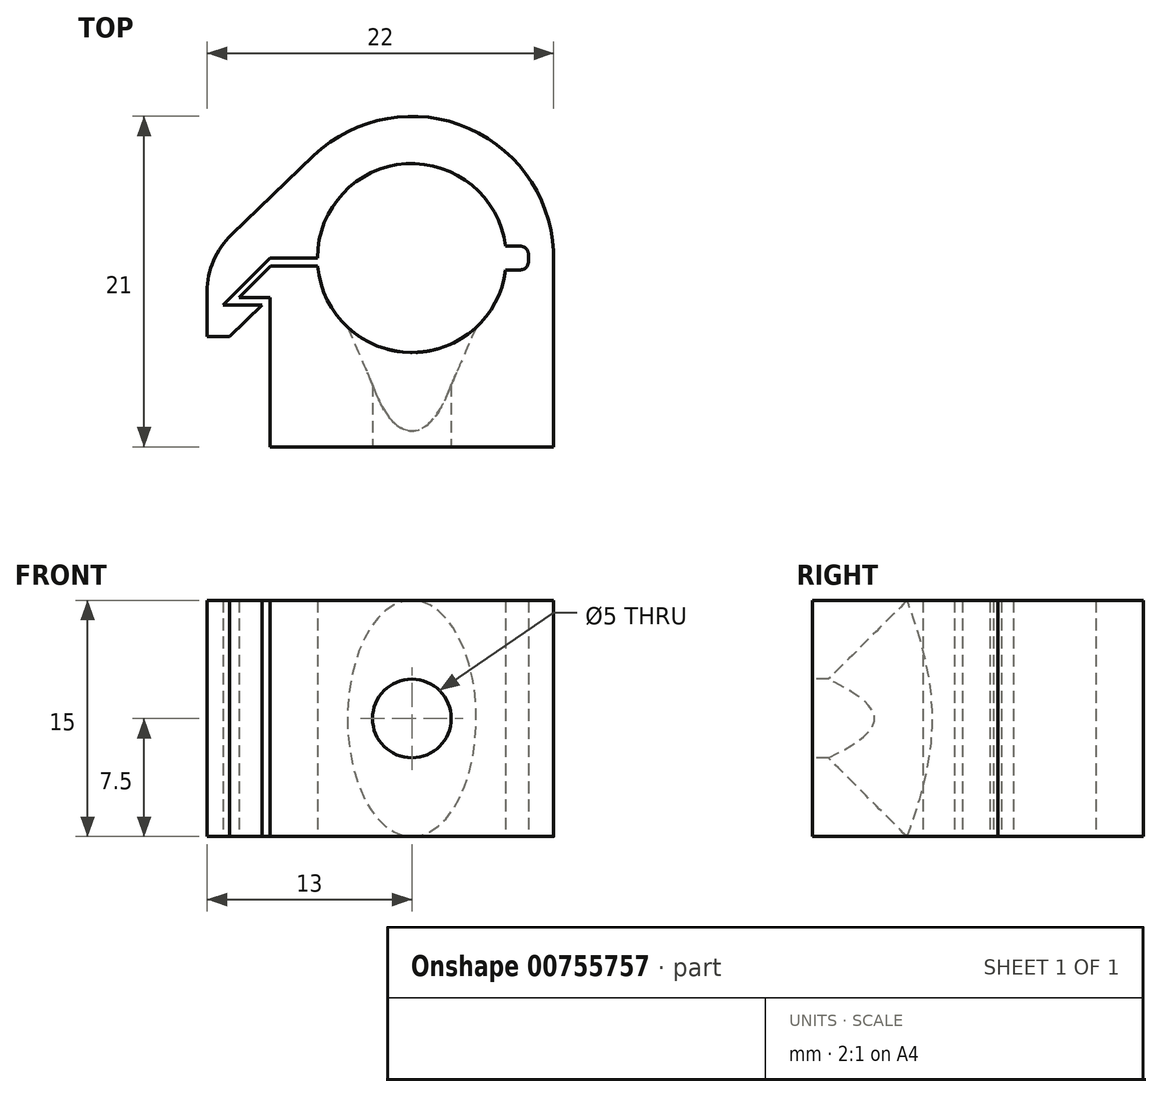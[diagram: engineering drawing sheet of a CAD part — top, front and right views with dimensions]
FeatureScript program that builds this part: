
annotation { "Feature Type Name" : "Feature", "Feature Type Description" : "" }
export const myFeature = defineFeature(function(context is Context, id is Id, definition is map)
    precondition{}
    {
        {
            var Q0;
            Q0=qCreatedBy(makeId("Top.planeOp"),FACE);
            var sketch = newSketch(context, id + "F0", { "sketchPlane" : qUnion([Q0])});
            skArc(sketch, "E0", {"start": v(-5.98, -0.5) * mm, "mid": v(-0.13, -6) * mm, "end": v(5.95, -0.75) * mm});
            skArc(sketch, "E1.0", {"start": v(9, -0.23) * mm, "mid": v(3.64, 8.23) * mm, "end": v(-6.23, 6.5) * mm});
            skLineSegment(sketch, "E2", {"start": v(-9, 0) * mm, "end": v(-6, 0) * mm});
            skLineSegment(sketch, "E3.0", {"start": v(-8.99, -0.5) * mm, "end": v(-5.98, -0.5) * mm});
            skLineSegment(sketch, "E4.top", {"start": v(-9, -12) * mm, "end": v(9, -12) * mm});
            skLineSegment(sketch, "E5.top", {"start": v(-8.99, -2.5) * mm, "end": v(-10.99, -2.5) * mm});
            skLineSegment(sketch, "E5.left", {"start": v(-8.99, -0.5) * mm, "end": v(-8.99, -2.5) * mm});
            skLineSegment(sketch, "E6", {"start": v(-8.99, -0.5) * mm, "end": v(-10.99, -2.5) * mm});
            skLineSegment(sketch, "E7.bottom", {"start": v(-9, 0) * mm, "end": v(-12.52, 0) * mm});
            skLineSegment(sketch, "E7.top", {"start": v(-11.57, -5) * mm, "end": v(-13, -5) * mm});
            skLineSegment(sketch, "E7.left", {"start": v(-9, -2.5) * mm, "end": v(-9, -12) * mm});
            skLineSegment(sketch, "E7.right", {"start": v(-13, -2.13) * mm, "end": v(-13, -5) * mm});
            skLineSegment(sketch, "E8", {"start": v(-9, 0) * mm, "end": v(-12, -3) * mm});
            skLineSegment(sketch, "E9", {"start": v(-11.46, 1.48) * mm, "end": v(-6.23, 6.5) * mm});
            skPoint(sketch, "E10.visualSharp", {"position": v(-13, 0) * mm});
            skArc(sketch, "E10.filletArc", {"start": v(-11.46, 1.48) * mm, "mid": v(-12.6, -0.17) * mm, "end": v(-13, -2.13) * mm});
            skLineSegment(sketch, "E11.bottom", {"start": v(6.9, -0.75) * mm, "end": v(5.95, -0.75) * mm});
            skLineSegment(sketch, "E11.top", {"start": v(6.9, 0.75) * mm, "end": v(5.95, 0.75) * mm});
            skLineSegment(sketch, "E11.left", {"start": v(7.4, -0.25) * mm, "end": v(7.4, 0.25) * mm});
            skPoint(sketch, "E12.visualSharp", {"position": v(7.4, 0.75) * mm});
            skArc(sketch, "E12.filletArc", {"start": v(7.4, 0.25) * mm, "mid": v(7.25, 0.6) * mm, "end": v(6.9, 0.75) * mm});
            skPoint(sketch, "E13.visualSharp", {"position": v(7.4, -0.75) * mm});
            skArc(sketch, "E13.filletArc", {"start": v(6.9, -0.75) * mm, "mid": v(7.25, -0.6) * mm, "end": v(7.4, -0.25) * mm});
            skArc(sketch, "E14.trimOffspring", {"start": v(5.95, 0.75) * mm, "mid": v(-0.38, 5.99) * mm, "end": v(-6, 0) * mm});
            skLineSegment(sketch, "E15", {"start": v(-9.5, -3) * mm, "end": v(-12, -3) * mm});
            skLineSegment(sketch, "E16", {"start": v(-9.5, -3) * mm, "end": v(-11.57, -5) * mm});
            skLineSegment(sketch, "E17", {"start": v(9, -0.23) * mm, "end": v(9, -12) * mm});
            skSolve(sketch);
        }
        {
            var Q0;
            Q0=makeQuery(id+"F0.imprint","IMPRINT",FACE,{"disambiguationData":[TD([[makeQuery(id+"F0.imprint","IMPRINT",EDGE,{"derivedFrom":sQuery(id+"F0.wireOp",EDGE,"E7.top")}),-1.0]])]});
            var Q1;
            {var subQ4=sQuery(id+"F0.wireOp",EDGE,"E4.top");Q1=makeQuery(id+"F0.imprint","IMPRINT",FACE,{"disambiguationData":[TD([[makeQuery(id+"F0.imprint","IMPRINT",EDGE,{"derivedFrom":subQ4}),1.0]])]});}
            var Q2;
            Q2=makeQuery(id+"F0.imprint","IMPRINT",FACE,{"disambiguationData":[TD([[makeQuery(id+"F0.imprint","IMPRINT",EDGE,{"derivedFrom":sQuery(id+"F0.wireOp",EDGE,"E0")}),-1.0]])]});
            var Q3;
            {var subQ0=sQuery(id+"F0.wireOp",EDGE,"LmTLJ9r3-tRaW-AbCN-yqt8-uPBCqrNAEFa4");var subQ1=sQuery(id+"F0.wireOp",EDGE,"E1.0");var subQ2=makeQuery(id+"F0.imprint","INTERSECT",VERTEX,{"disambiguationData":[OD(0.0)],"derivedFrom":[subQ1,subQ0]});Q3=makeQuery(id+"F0.imprint","IMPRINT",FACE,{"disambiguationData":[TD([[makeQuery(id+"F0.imprint","IMPRINT",EDGE,{"disambiguationData":[TD([[subQ2,1.0]])],"derivedFrom":subQ1}),1.0]])]});}
            var Q4;
            {var subQ0=sQuery(id+"F0.wireOp",EDGE,"E6");var subQ1=sQuery(id+"F0.wireOp",EDGE,"E5.top");var subQ2=makeQuery(id+"F0.imprint","INTERSECT",VERTEX,{"derivedFrom":[subQ1,subQ0]});Q4=makeQuery(id+"F0.imprint","IMPRINT",FACE,{"disambiguationData":[TD([[makeQuery(id+"F0.imprint","IMPRINT",EDGE,{"disambiguationData":[TD([[subQ2,1.0]])],"derivedFrom":subQ1}),-1.0]])]});}
            var Q5;
            {var subQ0=sQuery(id+"F0.wireOp",EDGE,"E5.left");Q5=makeQuery(id+"F0.imprint","IMPRINT",FACE,{"disambiguationData":[TD([[makeQuery(id+"F0.imprint","IMPRINT",EDGE,{"derivedFrom":subQ0}),-1.0]])]});}
            extrude(context, id + "F1", {"entities" : qUnion([Q0, Q1, Q2, Q3, Q4, Q5]), "depth" : 15 * mm, "offsetDistance" : 25 * mm, "symmetric" : true});
        }
        {
            var Q0;
            Q0=makeQuery(id+"F1.opExtrude","SWEPT_FACE",FACE,{"disambiguationData":[OSD([sQuery(id+"F0.wireOp",EDGE,"E4.top")])]});
            var sketch = newSketch(context, id + "F2", { "sketchPlane" : qUnion([Q0])});
            skCircle(sketch, "E18", {"center": v(0, 0) * mm, "radius": 2.5 * mm});
            skSolve(sketch);
        }
        {
            var Q0;
            Q0=makeQuery(id+"F2.imprint","IMPRINT",FACE,{"disambiguationData":[TD([[makeQuery(id+"F2.imprint","IMPRINT",EDGE,{"derivedFrom":sQuery(id+"F2.wireOp",EDGE,"E18")}),1.0]])]});
            extrude(context, id + "F3", {"entities" : qUnion([Q0]), "operationType" : NewBodyOperationType.REMOVE, "oppositeDirection" : true, "depth" : 10 * mm, "offsetDistance" : 25 * mm});
        }
        {
            var Q0;
            Q0=makeQuery(id+"F3.boolean.opBoolean","INTERSECT",EDGE,{"derivedFrom":[makeQuery(id+"F1.opExtrude","SWEPT_FACE",FACE,{"disambiguationData":[OSD([sQuery(id+"F0.wireOp",EDGE,"E0")])]}),makeQuery(id+"F3.opExtrude","SWEPT_FACE",FACE,{"disambiguationData":[OSD([sQuery(id+"F2.wireOp",EDGE,"E18")])]})]});
            chamfer(context, id + "F4", {"entities" : qUnion([Q0]), "width" : 5 * mm, "tangentPropagation" : true});
        }
    });
